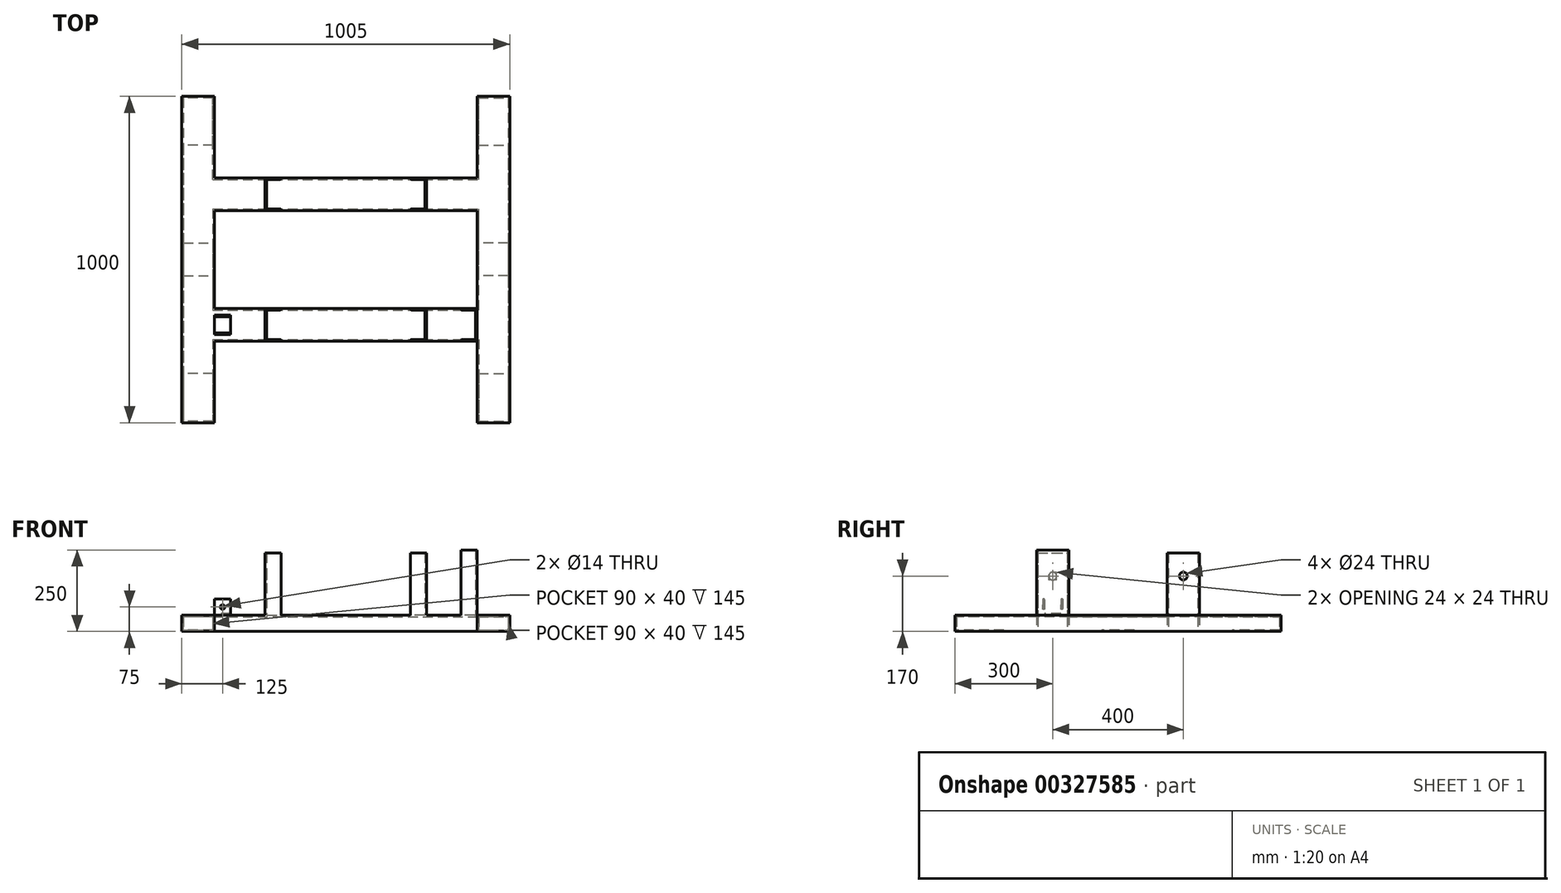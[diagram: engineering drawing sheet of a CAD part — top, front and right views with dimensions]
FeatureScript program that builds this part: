
annotation { "Feature Type Name" : "Feature", "Feature Type Description" : "" }
export const myFeature = defineFeature(function(context is Context, id is Id, definition is map)
    precondition{}
    {
        {
            var Q0;
            Q0=qCreatedBy(makeId("Top.planeOp"),FACE);
            var sketch = newSketch(context, id + "F0", { "sketchPlane" : qUnion([Q0])});
            skLineSegment(sketch, "E0", {"start": v(-402.5, 150) * mm, "end": v(402.5, 150) * mm});
            skLineSegment(sketch, "E1", {"start": v(0, 0) * mm, "end": v(0, 150) * mm, "construction": true});
            skPoint(sketch, "E2", {"position": v(0, 150) * mm});
            skLineSegment(sketch, "E3.0", {"start": v(-402.5, 250) * mm, "end": v(402.5, 250) * mm});
            skLineSegment(sketch, "E4", {"start": v(402.5, 0) * mm, "end": v(402.5, 500) * mm});
            skLineSegment(sketch, "E5", {"start": v(402.5, 500) * mm, "end": v(502.5, 500) * mm});
            skLineSegment(sketch, "E6", {"start": v(502.5, 500) * mm, "end": v(502.5, 0) * mm});
            skLineSegment(sketch, "E7.MirrorCS", {"start": v(-402.5, 0) * mm, "end": v(-402.5, 500) * mm});
            skLineSegment(sketch, "E8.MirrorCS", {"start": v(-502.5, 500) * mm, "end": v(-502.5, 0) * mm});
            skLineSegment(sketch, "E9.MirrorCS", {"start": v(-402.5, 500) * mm, "end": v(-502.5, 500) * mm});
            skLineSegment(sketch, "E10.MirrorCS", {"start": v(-402.5, 0) * mm, "end": v(-402.5, -500) * mm});
            skLineSegment(sketch, "E11.MirrorCS", {"start": v(-502.5, -500) * mm, "end": v(-502.5, 0) * mm});
            skLineSegment(sketch, "E12.MirrorCS", {"start": v(-402.5, -500) * mm, "end": v(-502.5, -500) * mm});
            skLineSegment(sketch, "E13.MirrorCS", {"start": v(-402.5, -250) * mm, "end": v(402.5, -250) * mm});
            skLineSegment(sketch, "E14.MirrorCS", {"start": v(-402.5, -150) * mm, "end": v(402.5, -150) * mm});
            skLineSegment(sketch, "E15.MirrorCS", {"start": v(402.5, 0) * mm, "end": v(402.5, -500) * mm});
            skLineSegment(sketch, "E16.MirrorCS", {"start": v(502.5, -500) * mm, "end": v(502.5, 0) * mm});
            skLineSegment(sketch, "E17.MirrorCS", {"start": v(402.5, -500) * mm, "end": v(502.5, -500) * mm});
            skLineSegment(sketch, "E18.bottom", {"start": v(502.5, 50) * mm, "end": v(402.5, 50) * mm});
            skLineSegment(sketch, "E18.top", {"start": v(502.5, -50) * mm, "end": v(402.5, -50) * mm});
            skLineSegment(sketch, "E18.left", {"start": v(502.5, 50) * mm, "end": v(502.5, -50) * mm});
            skLineSegment(sketch, "E18.right", {"start": v(402.5, 50) * mm, "end": v(402.5, -50) * mm});
            skPoint(sketch, "E18.middle", {"position": v(452.5, 0) * mm});
            skPoint(sketch, "E18.middle.positionSnap0", {"position": v(452.5, 500) * mm});
            skPoint(sketch, "E18.centerSnap0", {"position": v(452.5, 500) * mm});
            skLineSegment(sketch, "E19", {"start": v(402.5, 350) * mm, "end": v(502.5, 350) * mm});
            skLineSegment(sketch, "E20.MirrorCS", {"start": v(402.5, -350) * mm, "end": v(502.5, -350) * mm});
            skLineSegment(sketch, "E21.MirrorCS", {"start": v(-402.5, -350) * mm, "end": v(-502.5, -350) * mm});
            skLineSegment(sketch, "E22.MirrorCS", {"start": v(-502.5, -50) * mm, "end": v(-402.5, -50) * mm});
            skLineSegment(sketch, "E23.MirrorCS", {"start": v(-502.5, 50) * mm, "end": v(-402.5, 50) * mm});
            skLineSegment(sketch, "E24.MirrorCS", {"start": v(-402.5, 350) * mm, "end": v(-502.5, 350) * mm});
            skPoint(sketch, "E25.orphan", {"position": v(40.25, 250) * mm});
            skPoint(sketch, "E26.orphan", {"position": v(-40.25, 250) * mm});
            skPoint(sketch, "E27.orphan", {"position": v(40.25, -250) * mm});
            skPoint(sketch, "E28.orphan", {"position": v(-40.25, -250) * mm});
            skSolve(sketch);
        }
        {
            var Q0;
            Q0 = qSketchRegion(id + "F0", true);
            extrude(context, id + "F1", {"entities" : qUnion([Q0]), "depth" : 50 * mm});
        }
        {
            var Q0;
            Q0=makeQuery(id+"F1.opExtrude","CAP_FACE",FACE,{"disambiguationData":[OSD([sQuery(id+"F0.wireOp",EDGE,"E0"),sQuery(id+"F0.wireOp",EDGE,"E3.0"),sQuery(id+"F0.wireOp",EDGE,"E4"),sQuery(id+"F0.wireOp",EDGE,"E5"),sQuery(id+"F0.wireOp",EDGE,"E6"),sQuery(id+"F0.wireOp",EDGE,"E7.MirrorCS"),sQuery(id+"F0.wireOp",EDGE,"E8.MirrorCS"),sQuery(id+"F0.wireOp",EDGE,"E9.MirrorCS"),sQuery(id+"F0.wireOp",EDGE,"E10.MirrorCS"),sQuery(id+"F0.wireOp",EDGE,"E11.MirrorCS"),sQuery(id+"F0.wireOp",EDGE,"E12.MirrorCS"),sQuery(id+"F0.wireOp",EDGE,"E13.MirrorCS"),sQuery(id+"F0.wireOp",EDGE,"E14.MirrorCS"),sQuery(id+"F0.wireOp",EDGE,"E15.MirrorCS"),sQuery(id+"F0.wireOp",EDGE,"E16.MirrorCS"),sQuery(id+"F0.wireOp",EDGE,"E17.MirrorCS"),sQuery(id+"F0.wireOp",EDGE,"E18.left"),sQuery(id+"F0.wireOp",EDGE,"E18.right")])],"isStart":true});
            shell(context, id + "F2", {"entities" : qUnion([Q0]), "thickness" : 5 * mm});
        }
        {
            var Q0;
            {var subQ0=sQuery(id+"F0.wireOp",EDGE,"E12.MirrorCS");Q0=makeQuery(id+"F0.imprint","IMPRINT",FACE,{"disambiguationData":[TD([[makeQuery(id+"F0.imprint","IMPRINT",EDGE,{"derivedFrom":subQ0}),-1.0]])]});}
            var Q1;
            {var subQ3=sQuery(id+"F0.wireOp",EDGE,"E22.MirrorCS");Q1=makeQuery(id+"F0.imprint","IMPRINT",FACE,{"disambiguationData":[TD([[makeQuery(id+"F0.imprint","IMPRINT",EDGE,{"derivedFrom":subQ3}),1.0]])]});}
            var Q2;
            {var subQ0=sQuery(id+"F0.wireOp",EDGE,"E9.MirrorCS");Q2=makeQuery(id+"F0.imprint","IMPRINT",FACE,{"disambiguationData":[TD([[makeQuery(id+"F0.imprint","IMPRINT",EDGE,{"derivedFrom":subQ0}),1.0]])]});}
            var Q3;
            {var subQ0=sQuery(id+"F0.wireOp",EDGE,"E17.MirrorCS");Q3=makeQuery(id+"F0.imprint","IMPRINT",FACE,{"disambiguationData":[TD([[makeQuery(id+"F0.imprint","IMPRINT",EDGE,{"derivedFrom":subQ0}),1.0]])]});}
            var Q4;
            Q4=makeQuery(id+"F0.imprint","IMPRINT",FACE,{"disambiguationData":[TD([[makeQuery(id+"F0.imprint","IMPRINT",EDGE,{"derivedFrom":sQuery(id+"F0.wireOp",EDGE,"E18.bottom")}),1.0]])]});
            var Q5;
            {var subQ0=sQuery(id+"F0.wireOp",EDGE,"E5");Q5=makeQuery(id+"F0.imprint","IMPRINT",FACE,{"disambiguationData":[TD([[makeQuery(id+"F0.imprint","IMPRINT",EDGE,{"derivedFrom":subQ0}),-1.0]])]});}
            extrude(context, id + "F3", {"entities" : qUnion([Q0, Q1, Q2, Q3, Q4, Q5]), "operationType" : NewBodyOperationType.ADD, "depth" : 5 * mm});
        }
        {
            var Q0;
            Q0=makeQuery(id+"F1.opExtrude","CAP_FACE",FACE,{"disambiguationData":[OSD([sQuery(id+"F0.wireOp",EDGE,"E0"),sQuery(id+"F0.wireOp",EDGE,"E3.0"),sQuery(id+"F0.wireOp",EDGE,"E4"),sQuery(id+"F0.wireOp",EDGE,"E5"),sQuery(id+"F0.wireOp",EDGE,"E6"),sQuery(id+"F0.wireOp",EDGE,"E7.MirrorCS"),sQuery(id+"F0.wireOp",EDGE,"E8.MirrorCS"),sQuery(id+"F0.wireOp",EDGE,"E9.MirrorCS"),sQuery(id+"F0.wireOp",EDGE,"E10.MirrorCS"),sQuery(id+"F0.wireOp",EDGE,"E11.MirrorCS"),sQuery(id+"F0.wireOp",EDGE,"E12.MirrorCS"),sQuery(id+"F0.wireOp",EDGE,"E13.MirrorCS"),sQuery(id+"F0.wireOp",EDGE,"E14.MirrorCS"),sQuery(id+"F0.wireOp",EDGE,"E15.MirrorCS"),sQuery(id+"F0.wireOp",EDGE,"E16.MirrorCS"),sQuery(id+"F0.wireOp",EDGE,"E17.MirrorCS"),sQuery(id+"F0.wireOp",EDGE,"E18.left"),sQuery(id+"F0.wireOp",EDGE,"E18.right")])],"isStart":false});
            var sketch = newSketch(context, id + "F4", { "sketchPlane" : qUnion([Q0])});
            skLineSegment(sketch, "E29.bottom", {"start": v(248, 250) * mm, "end": v(-248, 250) * mm, "construction": true});
            skLineSegment(sketch, "E29.top", {"start": v(198, -250) * mm, "end": v(-248, -250) * mm, "construction": true});
            skLineSegment(sketch, "E29.left", {"start": v(248, 250) * mm, "end": v(248, -150) * mm, "construction": true});
            skLineSegment(sketch, "E29.right", {"start": v(-248, 250) * mm, "end": v(-248, -250) * mm, "construction": true});
            skPoint(sketch, "E29.middle", {"position": v(0, 0) * mm});
            skLineSegment(sketch, "E30.bottom", {"start": v(248, -250) * mm, "end": v(198, -250) * mm});
            skLineSegment(sketch, "E30.top", {"start": v(248, -150) * mm, "end": v(198, -150) * mm});
            skLineSegment(sketch, "E30.left", {"start": v(248, -250) * mm, "end": v(248, -150) * mm});
            skLineSegment(sketch, "E30.right", {"start": v(198, -250) * mm, "end": v(198, -249) * mm});
            skLineSegment(sketch, "E31.0", {"start": v(243, -155) * mm, "end": v(202, -155) * mm});
            skLineSegment(sketch, "E31.1", {"start": v(243, -245) * mm, "end": v(243, -155) * mm});
            skLineSegment(sketch, "E31.2", {"start": v(243, -245) * mm, "end": v(202, -245) * mm});
            skLineSegment(sketch, "E32.trimOffspring", {"start": v(198, -151) * mm, "end": v(198, -150) * mm});
            skPoint(sketch, "E33.visualSharp", {"position": v(198, -155) * mm});
            skArc(sketch, "E33.filletArc", {"start": v(198, -151) * mm, "mid": v(199.17, -153.83) * mm, "end": v(202, -155) * mm});
            skPoint(sketch, "E34.visualSharp", {"position": v(198, -245) * mm});
            skArc(sketch, "E34.filletArc", {"start": v(202, -245) * mm, "mid": v(199.17, -246.17) * mm, "end": v(198, -249) * mm});
            skSolve(sketch);
        }
        {
            var Q0;
            Q0 = qSketchRegion(id + "F4", true);
            extrude(context, id + "F5", {"entities" : qUnion([Q0]), "depth" : 190 * mm});
        }
        {
            var Q0;
            Q0=makeQuery(id+"F5.opExtrude","SWEPT_FACE",FACE,{"disambiguationData":[OSD([sQuery(id+"F4.wireOp",EDGE,"E30.left")])]});
            var sketch = newSketch(context, id + "F6", { "sketchPlane" : qUnion([Q0])});
            skLineSegment(sketch, "E35", {"start": v(-200, 50) * mm, "end": v(-200, 240) * mm, "construction": true});
            skPoint(sketch, "E36", {"position": v(-200, 170) * mm});
            skSolve(sketch);
        }
        {
            var Q0;
            Q0=sQuery(id+"F6.wireOp",VERTEX,"E36");
            var Q1;
            Q1=makeQuery(id+"F5.opExtrude","SWEPT_BODY",BODY,{"disambiguationData":[OSD([sQuery(id+"F4.wireOp",EDGE,"E30.bottom"),sQuery(id+"F4.wireOp",EDGE,"E30.top"),sQuery(id+"F4.wireOp",EDGE,"E30.left"),sQuery(id+"F4.wireOp",EDGE,"E30.right"),sQuery(id+"F4.wireOp",EDGE,"E31.0"),sQuery(id+"F4.wireOp",EDGE,"E31.1"),sQuery(id+"F4.wireOp",EDGE,"E31.2"),sQuery(id+"F4.wireOp",EDGE,"E32.trimOffspring"),sQuery(id+"F4.wireOp",EDGE,"E33.filletArc"),sQuery(id+"F4.wireOp",EDGE,"E34.filletArc")])]});
            hole(context, id + "F7", {"style" : HoleStyle.SIMPLE, "endStyle" : HoleEndStyle.THROUGH, "holeDiameter" : 24 * mm, "tappedDepth" : 12 * mm, "tapClearance" : 3, "locations" : qUnion([Q0]), "scope" : qUnion([Q1])});
        }
        {
            var Q0;
            Q0=makeQuery(id+"F5.opExtrude","SWEPT_BODY",BODY,{"disambiguationData":[OSD([sQuery(id+"F4.wireOp",EDGE,"E30.bottom"),sQuery(id+"F4.wireOp",EDGE,"E30.top"),sQuery(id+"F4.wireOp",EDGE,"E30.left"),sQuery(id+"F4.wireOp",EDGE,"E30.right"),sQuery(id+"F4.wireOp",EDGE,"E31.0"),sQuery(id+"F4.wireOp",EDGE,"E31.1"),sQuery(id+"F4.wireOp",EDGE,"E31.2"),sQuery(id+"F4.wireOp",EDGE,"E32.trimOffspring"),sQuery(id+"F4.wireOp",EDGE,"E33.filletArc"),sQuery(id+"F4.wireOp",EDGE,"E34.filletArc")])]});
            var Q1;
            Q1=qCreatedBy(makeId("Right.planeOp"),FACE);
            mirror(context, id + "F8", {"entities" : qUnion([Q0]), "mirrorPlane" : qUnion([Q1])});
        }
        {
            var Q0;
            Q0=makeQuery(id+"F5.opExtrude","SWEPT_BODY",BODY,{"disambiguationData":[OSD([sQuery(id+"F4.wireOp",EDGE,"E30.bottom"),sQuery(id+"F4.wireOp",EDGE,"E30.top"),sQuery(id+"F4.wireOp",EDGE,"E30.left"),sQuery(id+"F4.wireOp",EDGE,"E30.right"),sQuery(id+"F4.wireOp",EDGE,"E31.0"),sQuery(id+"F4.wireOp",EDGE,"E31.1"),sQuery(id+"F4.wireOp",EDGE,"E31.2"),sQuery(id+"F4.wireOp",EDGE,"E32.trimOffspring"),sQuery(id+"F4.wireOp",EDGE,"E33.filletArc"),sQuery(id+"F4.wireOp",EDGE,"E34.filletArc")])]});
            var Q1;
            Q1=makeQuery(id+"F8.opPattern","COPY",BODY,{"derivedFrom":makeQuery(id+"F5.opExtrude","SWEPT_BODY",BODY,{"disambiguationData":[OSD([sQuery(id+"F4.wireOp",EDGE,"E30.bottom"),sQuery(id+"F4.wireOp",EDGE,"E30.top"),sQuery(id+"F4.wireOp",EDGE,"E30.left"),sQuery(id+"F4.wireOp",EDGE,"E30.right"),sQuery(id+"F4.wireOp",EDGE,"E31.0"),sQuery(id+"F4.wireOp",EDGE,"E31.1"),sQuery(id+"F4.wireOp",EDGE,"E31.2"),sQuery(id+"F4.wireOp",EDGE,"E32.trimOffspring"),sQuery(id+"F4.wireOp",EDGE,"E33.filletArc"),sQuery(id+"F4.wireOp",EDGE,"E34.filletArc")])]}),"instanceName":"1"});
            var Q2;
            Q2=qCreatedBy(makeId("Front.planeOp"),FACE);
            mirror(context, id + "F9", {"entities" : qUnion([Q0, Q1]), "mirrorPlane" : qUnion([Q2])});
        }
        {
            var Q0;
            Q0=makeQuery(id+"F8.opPattern","COPY",BODY,{"derivedFrom":makeQuery(id+"F5.opExtrude","SWEPT_BODY",BODY,{"disambiguationData":[OSD([sQuery(id+"F4.wireOp",EDGE,"E30.bottom"),sQuery(id+"F4.wireOp",EDGE,"E30.top"),sQuery(id+"F4.wireOp",EDGE,"E30.left"),sQuery(id+"F4.wireOp",EDGE,"E30.right"),sQuery(id+"F4.wireOp",EDGE,"E31.0"),sQuery(id+"F4.wireOp",EDGE,"E31.1"),sQuery(id+"F4.wireOp",EDGE,"E31.2"),sQuery(id+"F4.wireOp",EDGE,"E32.trimOffspring"),sQuery(id+"F4.wireOp",EDGE,"E33.filletArc"),sQuery(id+"F4.wireOp",EDGE,"E34.filletArc")])]}),"instanceName":"1"});
            var Q1;
            Q1=makeQuery(id+"F9.opPattern","COPY",BODY,{"derivedFrom":makeQuery(id+"F8.opPattern","COPY",BODY,{"derivedFrom":makeQuery(id+"F5.opExtrude","SWEPT_BODY",BODY,{"disambiguationData":[OSD([sQuery(id+"F4.wireOp",EDGE,"E30.bottom"),sQuery(id+"F4.wireOp",EDGE,"E30.top"),sQuery(id+"F4.wireOp",EDGE,"E30.left"),sQuery(id+"F4.wireOp",EDGE,"E30.right"),sQuery(id+"F4.wireOp",EDGE,"E31.0"),sQuery(id+"F4.wireOp",EDGE,"E31.1"),sQuery(id+"F4.wireOp",EDGE,"E31.2"),sQuery(id+"F4.wireOp",EDGE,"E32.trimOffspring"),sQuery(id+"F4.wireOp",EDGE,"E33.filletArc"),sQuery(id+"F4.wireOp",EDGE,"E34.filletArc")])]}),"instanceName":"1"}),"instanceName":"1"});
            var Q2;
            Q2=makeQuery(id+"F5.opExtrude","SWEPT_BODY",BODY,{"disambiguationData":[OSD([sQuery(id+"F4.wireOp",EDGE,"E30.bottom"),sQuery(id+"F4.wireOp",EDGE,"E30.top"),sQuery(id+"F4.wireOp",EDGE,"E30.left"),sQuery(id+"F4.wireOp",EDGE,"E30.right"),sQuery(id+"F4.wireOp",EDGE,"E31.0"),sQuery(id+"F4.wireOp",EDGE,"E31.1"),sQuery(id+"F4.wireOp",EDGE,"E31.2"),sQuery(id+"F4.wireOp",EDGE,"E32.trimOffspring"),sQuery(id+"F4.wireOp",EDGE,"E33.filletArc"),sQuery(id+"F4.wireOp",EDGE,"E34.filletArc")])]});
            var Q3;
            Q3=makeQuery(id+"F9.opPattern","COPY",BODY,{"derivedFrom":makeQuery(id+"F5.opExtrude","SWEPT_BODY",BODY,{"disambiguationData":[OSD([sQuery(id+"F4.wireOp",EDGE,"E30.bottom"),sQuery(id+"F4.wireOp",EDGE,"E30.top"),sQuery(id+"F4.wireOp",EDGE,"E30.left"),sQuery(id+"F4.wireOp",EDGE,"E30.right"),sQuery(id+"F4.wireOp",EDGE,"E31.0"),sQuery(id+"F4.wireOp",EDGE,"E31.1"),sQuery(id+"F4.wireOp",EDGE,"E31.2"),sQuery(id+"F4.wireOp",EDGE,"E32.trimOffspring"),sQuery(id+"F4.wireOp",EDGE,"E33.filletArc"),sQuery(id+"F4.wireOp",EDGE,"E34.filletArc")])]}),"instanceName":"1"});
            var Q4;
            Q4=makeQuery(id+"F1.opExtrude","SWEPT_BODY",BODY,{"disambiguationData":[OSD([sQuery(id+"F0.wireOp",EDGE,"E0"),sQuery(id+"F0.wireOp",EDGE,"E3.0"),sQuery(id+"F0.wireOp",EDGE,"E4"),sQuery(id+"F0.wireOp",EDGE,"E5"),sQuery(id+"F0.wireOp",EDGE,"E6"),sQuery(id+"F0.wireOp",EDGE,"E7.MirrorCS"),sQuery(id+"F0.wireOp",EDGE,"E8.MirrorCS"),sQuery(id+"F0.wireOp",EDGE,"E9.MirrorCS"),sQuery(id+"F0.wireOp",EDGE,"E10.MirrorCS"),sQuery(id+"F0.wireOp",EDGE,"E11.MirrorCS"),sQuery(id+"F0.wireOp",EDGE,"E12.MirrorCS"),sQuery(id+"F0.wireOp",EDGE,"E13.MirrorCS"),sQuery(id+"F0.wireOp",EDGE,"E14.MirrorCS"),sQuery(id+"F0.wireOp",EDGE,"E15.MirrorCS"),sQuery(id+"F0.wireOp",EDGE,"E16.MirrorCS"),sQuery(id+"F0.wireOp",EDGE,"E17.MirrorCS"),sQuery(id+"F0.wireOp",EDGE,"E18.left"),sQuery(id+"F0.wireOp",EDGE,"E18.right")])]});
            booleanBodies(context, id + "F10", {"operationType" : BooleanOperationType.UNION, "tools" : qUnion([Q0, Q1, Q2, Q3, Q4])});
        }
        {
            var Q0;
            {var subQ0=sQuery(id+"F0.wireOp",EDGE,"E14.MirrorCS");var subQ1=sQuery(id+"F0.wireOp",EDGE,"E12.MirrorCS");var subQ4=sQuery(id+"F0.wireOp",EDGE,"E10.MirrorCS");var subQ5=sQuery(id+"F0.wireOp",EDGE,"E11.MirrorCS");var subQ6=sQuery(id+"F0.wireOp",EDGE,"E8.MirrorCS");var subQ9=sQuery(id+"F0.wireOp",EDGE,"E9.MirrorCS");var subQ10=sQuery(id+"F0.wireOp",EDGE,"E0");var subQ11=sQuery(id+"F0.wireOp",EDGE,"E13.MirrorCS");var subQ12=sQuery(id+"F0.wireOp",EDGE,"E3.0");var subQ13=sQuery(id+"F0.wireOp",EDGE,"E7.MirrorCS");Q0=makeQuery(id+"F10.opBoolean","SPLIT",FACE,{"disambiguationData":[TD([makeQuery(id+"F1.opExtrude","SWEPT_FACE",FACE,{"disambiguationData":[OSD([subQ13])]})])],"derivedFrom":makeQuery(id+"F1.opExtrude","CAP_FACE",FACE,{"disambiguationData":[OSD([subQ10,subQ12,sQuery(id+"F0.wireOp",EDGE,"E4"),sQuery(id+"F0.wireOp",EDGE,"E5"),sQuery(id+"F0.wireOp",EDGE,"E6"),subQ13,subQ6,subQ9,subQ4,subQ5,subQ1,subQ11,subQ0,sQuery(id+"F0.wireOp",EDGE,"E15.MirrorCS"),sQuery(id+"F0.wireOp",EDGE,"E16.MirrorCS"),sQuery(id+"F0.wireOp",EDGE,"E17.MirrorCS"),sQuery(id+"F0.wireOp",EDGE,"E18.left"),sQuery(id+"F0.wireOp",EDGE,"E18.right")])],"isStart":false})});}
            var sketch = newSketch(context, id + "F11", { "sketchPlane" : qUnion([Q0])});
            skLineSegment(sketch, "E37.bottom", {"start": v(-352.5, -170) * mm, "end": v(-402.5, -170) * mm});
            skLineSegment(sketch, "E37.top", {"start": v(-352.5, -230) * mm, "end": v(-402.5, -230) * mm});
            skLineSegment(sketch, "E37.left", {"start": v(-352.5, -170) * mm, "end": v(-352.5, -230) * mm});
            skLineSegment(sketch, "E37.right", {"start": v(-402.5, -170) * mm, "end": v(-402.5, -230) * mm});
            skPoint(sketch, "E37.middle", {"position": v(-377.5, -200) * mm});
            skPoint(sketch, "E37.middle.positionSnap0", {"position": v(-248, -200) * mm});
            skPoint(sketch, "E37.centerSnap0", {"position": v(-248, -200) * mm});
            skLineSegment(sketch, "E38.0", {"start": v(-352.5, -175) * mm, "end": v(-402.5, -175) * mm});
            skLineSegment(sketch, "E39.0", {"start": v(-352.5, -225) * mm, "end": v(-402.5, -225) * mm});
            skPoint(sketch, "E40.firstSnap0", {"position": v(-325.25, -150) * mm});
            skPoint(sketch, "E40.oppositeSnap0", {"position": v(-325.25, -250) * mm});
            skLineSegment(sketch, "E40.bottom", {"start": v(402.5, -150) * mm, "end": v(352.5, -150) * mm});
            skLineSegment(sketch, "E40.top", {"start": v(402.5, -250) * mm, "end": v(352.5, -250) * mm});
            skLineSegment(sketch, "E40.left", {"start": v(402.5, -150) * mm, "end": v(402.5, -250) * mm});
            skLineSegment(sketch, "E40.right", {"start": v(352.5, -150) * mm, "end": v(352.5, -151) * mm});
            skLineSegment(sketch, "E41.0", {"start": v(397.5, -155) * mm, "end": v(356.5, -155) * mm});
            skLineSegment(sketch, "E41.1", {"start": v(397.5, -155) * mm, "end": v(397.5, -245) * mm});
            skLineSegment(sketch, "E41.2", {"start": v(397.5, -245) * mm, "end": v(356.5, -245) * mm});
            skLineSegment(sketch, "E42.trimOffspring", {"start": v(352.5, -249) * mm, "end": v(352.5, -250) * mm});
            skPoint(sketch, "E43.visualSharp", {"position": v(352.5, -155) * mm});
            skArc(sketch, "E43.filletArc", {"start": v(352.5, -151) * mm, "mid": v(353.67, -153.83) * mm, "end": v(356.5, -155) * mm});
            skPoint(sketch, "E44.visualSharp", {"position": v(352.5, -245) * mm});
            skArc(sketch, "E44.filletArc", {"start": v(356.5, -245) * mm, "mid": v(353.67, -246.17) * mm, "end": v(352.5, -249) * mm});
            skSolve(sketch);
        }
        {
            var Q0;
            {var subQ0=sQuery(id+"F11.wireOp",EDGE,"E38.0");Q0=makeQuery(id+"F11.imprint","IMPRINT",FACE,{"disambiguationData":[TD([[makeQuery(id+"F11.imprint","IMPRINT",EDGE,{"derivedFrom":subQ0}),1.0]])]});}
            extrude(context, id + "F12", {"entities" : qUnion([Q0]), "operationType" : NewBodyOperationType.ADD, "depth" : 5 * mm});
        }
        {
            var Q0;
            {var subQ0=sQuery(id+"F11.wireOp",EDGE,"E37.top");Q0=makeQuery(id+"F11.imprint","IMPRINT",FACE,{"disambiguationData":[TD([[makeQuery(id+"F11.imprint","IMPRINT",EDGE,{"derivedFrom":subQ0}),-1.0]])]});}
            var Q1;
            {var subQ0=sQuery(id+"F11.wireOp",EDGE,"E37.bottom");Q1=makeQuery(id+"F11.imprint","IMPRINT",FACE,{"disambiguationData":[TD([[makeQuery(id+"F11.imprint","IMPRINT",EDGE,{"derivedFrom":subQ0}),1.0]])]});}
            extrude(context, id + "F13", {"entities" : qUnion([Q0, Q1]), "operationType" : NewBodyOperationType.ADD, "depth" : 50 * mm});
        }
        {
            var Q0;
            Q0=makeQuery(id+"F11.imprint","IMPRINT",FACE,{"disambiguationData":[TD([[makeQuery(id+"F11.imprint","IMPRINT",EDGE,{"derivedFrom":sQuery(id+"F11.wireOp",EDGE,"E40.bottom")}),1.0]])]});
            extrude(context, id + "F14", {"entities" : qUnion([Q0]), "operationType" : NewBodyOperationType.ADD, "depth" : 200 * mm});
        }
        {
            var Q0;
            Q0=makeQuery(id+"F13.opExtrude","SWEPT_FACE",FACE,{"disambiguationData":[OSD([sQuery(id+"F11.wireOp",EDGE,"E37.top")])]});
            var sketch = newSketch(context, id + "F15", { "sketchPlane" : qUnion([Q0])});
            skPoint(sketch, "E45", {"position": v(-377.5, 75) * mm});
            skPoint(sketch, "E45.positionSnap0", {"position": v(-402.5, 75) * mm});
            skPoint(sketch, "E45.positionSnap1", {"position": v(-377.5, 50) * mm});
            skSolve(sketch);
        }
        {
            var Q0;
            Q0=sQuery(id+"F15.wireOp",VERTEX,"E45");
            var Q1;
            Q1=makeQuery(id+"F8.opPattern","COPY",BODY,{"derivedFrom":makeQuery(id+"F5.opExtrude","SWEPT_BODY",BODY,{"disambiguationData":[OSD([sQuery(id+"F4.wireOp",EDGE,"E30.bottom"),sQuery(id+"F4.wireOp",EDGE,"E30.top"),sQuery(id+"F4.wireOp",EDGE,"E30.left"),sQuery(id+"F4.wireOp",EDGE,"E30.right"),sQuery(id+"F4.wireOp",EDGE,"E31.0"),sQuery(id+"F4.wireOp",EDGE,"E31.1"),sQuery(id+"F4.wireOp",EDGE,"E31.2"),sQuery(id+"F4.wireOp",EDGE,"E32.trimOffspring"),sQuery(id+"F4.wireOp",EDGE,"E33.filletArc"),sQuery(id+"F4.wireOp",EDGE,"E34.filletArc")])]}),"instanceName":"1"});
            hole(context, id + "F16", {"style" : HoleStyle.SIMPLE, "endStyle" : HoleEndStyle.THROUGH, "holeDiameter" : 14 * mm, "tappedDepth" : 12 * mm, "tapClearance" : 3, "locations" : qUnion([Q0]), "scope" : qUnion([Q1])});
        }
        {
            var Q0;
            Q0=makeQuery(id+"F12.opExtrude","CAP_EDGE",EDGE,{"disambiguationData":[OSD([sQuery(id+"F11.wireOp",EDGE,"E38.0")])],"isStart":false});
            var Q1;
            Q1=makeQuery(id+"F12.opExtrude","CAP_EDGE",EDGE,{"disambiguationData":[OSD([sQuery(id+"F11.wireOp",EDGE,"E39.0")])],"isStart":false});
            var Q2;
            Q2=makeQuery(id+"F13.opExtrude","CAP_EDGE",EDGE,{"disambiguationData":[OSD([sQuery(id+"F11.wireOp",EDGE,"E39.0")])],"isStart":false});
            var Q3;
            Q3=makeQuery(id+"F13.opExtrude","CAP_EDGE",EDGE,{"disambiguationData":[OSD([sQuery(id+"F11.wireOp",EDGE,"E38.0")])],"isStart":false});
            var Q4;
            Q4=makeQuery(id+"F13.opExtrude","CAP_EDGE",EDGE,{"disambiguationData":[OSD([sQuery(id+"F11.wireOp",EDGE,"E37.top")])],"isStart":true});
            var Q5;
            {var subQ0=sQuery(id+"F11.wireOp",EDGE,"E37.right");Q5=makeQuery(id+"F13.boolean.opBoolean","MERGE",EDGE,{"derivedFrom":[makeQuery(id+"F12.opExtrude","CAP_EDGE",EDGE,{"disambiguationData":[OSD([subQ0])],"isStart":true}),makeQuery(id+"F13.opExtrude","CAP_EDGE",EDGE,{"disambiguationData":[OSD([subQ0]),TDD([makeQuery(id+"F11.imprint","IMPRINT",EDGE,{"disambiguationData":[TD([[makeQuery(id+"F11.imprint","INTERSECT",VERTEX,{"derivedFrom":[sQuery(id+"F11.wireOp",EDGE,"E37.bottom"),subQ0]}),-1.0]])],"derivedFrom":subQ0})])],"isStart":true}),makeQuery(id+"F13.opExtrude","CAP_EDGE",EDGE,{"disambiguationData":[OSD([subQ0]),TDD([makeQuery(id+"F11.imprint","IMPRINT",EDGE,{"disambiguationData":[TD([[makeQuery(id+"F11.imprint","INTERSECT",VERTEX,{"derivedFrom":[sQuery(id+"F11.wireOp",EDGE,"E37.top"),subQ0]}),1.0]])],"derivedFrom":subQ0})])],"isStart":true})]});}
            var Q6;
            Q6=makeQuery(id+"F13.opExtrude","CAP_EDGE",EDGE,{"disambiguationData":[OSD([sQuery(id+"F11.wireOp",EDGE,"E37.bottom")])],"isStart":true});
            var Q7;
            {var subQ0=sQuery(id+"F11.wireOp",EDGE,"E37.left");Q7=makeQuery(id+"F13.boolean.opBoolean","MERGE",EDGE,{"derivedFrom":[makeQuery(id+"F12.opExtrude","CAP_EDGE",EDGE,{"disambiguationData":[OSD([subQ0])],"isStart":true}),makeQuery(id+"F13.opExtrude","CAP_EDGE",EDGE,{"disambiguationData":[OSD([subQ0]),TDD([makeQuery(id+"F11.imprint","IMPRINT",EDGE,{"disambiguationData":[TD([[makeQuery(id+"F11.imprint","INTERSECT",VERTEX,{"derivedFrom":[sQuery(id+"F11.wireOp",EDGE,"E37.bottom"),subQ0]}),-1.0]])],"derivedFrom":subQ0})])],"isStart":true}),makeQuery(id+"F13.opExtrude","CAP_EDGE",EDGE,{"disambiguationData":[OSD([subQ0]),TDD([makeQuery(id+"F11.imprint","IMPRINT",EDGE,{"disambiguationData":[TD([[makeQuery(id+"F11.imprint","INTERSECT",VERTEX,{"derivedFrom":[sQuery(id+"F11.wireOp",EDGE,"E37.top"),subQ0]}),1.0]])],"derivedFrom":subQ0})])],"isStart":true})]});}
            var Q8;
            Q8=makeQuery(id+"F8.opPattern","COPY",EDGE,{"derivedFrom":makeQuery(id+"F5.opExtrude","CAP_EDGE",EDGE,{"disambiguationData":[OSD([sQuery(id+"F4.wireOp",EDGE,"E30.left")])],"isStart":true}),"instanceName":"1"});
            var Q9;
            Q9=makeQuery(id+"F9.opPattern","COPY",EDGE,{"derivedFrom":makeQuery(id+"F8.opPattern","COPY",EDGE,{"derivedFrom":makeQuery(id+"F5.opExtrude","CAP_EDGE",EDGE,{"disambiguationData":[OSD([sQuery(id+"F4.wireOp",EDGE,"E30.left")])],"isStart":true}),"instanceName":"1"}),"instanceName":"1"});
            var Q10;
            Q10=makeQuery(id+"F5.opExtrude","CAP_EDGE",EDGE,{"disambiguationData":[OSD([sQuery(id+"F4.wireOp",EDGE,"E31.1")])],"isStart":true});
            var Q11;
            Q11=makeQuery(id+"F5.opExtrude","CAP_EDGE",EDGE,{"disambiguationData":[OSD([sQuery(id+"F4.wireOp",EDGE,"E31.0")])],"isStart":true});
            var Q12;
            Q12=makeQuery(id+"F5.opExtrude","CAP_EDGE",EDGE,{"disambiguationData":[OSD([sQuery(id+"F4.wireOp",EDGE,"E33.filletArc")])],"isStart":true});
            var Q13;
            Q13=makeQuery(id+"F5.opExtrude","CAP_EDGE",EDGE,{"disambiguationData":[OSD([sQuery(id+"F4.wireOp",EDGE,"E31.2")])],"isStart":true});
            var Q14;
            Q14=makeQuery(id+"F5.opExtrude","CAP_EDGE",EDGE,{"disambiguationData":[OSD([sQuery(id+"F4.wireOp",EDGE,"E34.filletArc")])],"isStart":true});
            var Q15;
            Q15=makeQuery(id+"F9.opPattern","COPY",EDGE,{"derivedFrom":makeQuery(id+"F5.opExtrude","CAP_EDGE",EDGE,{"disambiguationData":[OSD([sQuery(id+"F4.wireOp",EDGE,"E31.2")])],"isStart":true}),"instanceName":"1"});
            var Q16;
            Q16=makeQuery(id+"F9.opPattern","COPY",EDGE,{"derivedFrom":makeQuery(id+"F5.opExtrude","CAP_EDGE",EDGE,{"disambiguationData":[OSD([sQuery(id+"F4.wireOp",EDGE,"E34.filletArc")])],"isStart":true}),"instanceName":"1"});
            var Q17;
            Q17=makeQuery(id+"F9.opPattern","COPY",EDGE,{"derivedFrom":makeQuery(id+"F5.opExtrude","CAP_EDGE",EDGE,{"disambiguationData":[OSD([sQuery(id+"F4.wireOp",EDGE,"E31.1")])],"isStart":true}),"instanceName":"1"});
            var Q18;
            Q18=makeQuery(id+"F9.opPattern","COPY",EDGE,{"derivedFrom":makeQuery(id+"F5.opExtrude","CAP_EDGE",EDGE,{"disambiguationData":[OSD([sQuery(id+"F4.wireOp",EDGE,"E31.0")])],"isStart":true}),"instanceName":"1"});
            var Q19;
            Q19=makeQuery(id+"F9.opPattern","COPY",EDGE,{"derivedFrom":makeQuery(id+"F5.opExtrude","CAP_EDGE",EDGE,{"disambiguationData":[OSD([sQuery(id+"F4.wireOp",EDGE,"E33.filletArc")])],"isStart":true}),"instanceName":"1"});
            var Q20;
            Q20=makeQuery(id+"F9.opPattern","COPY",EDGE,{"derivedFrom":makeQuery(id+"F5.opExtrude","CAP_EDGE",EDGE,{"disambiguationData":[OSD([sQuery(id+"F4.wireOp",EDGE,"E30.left")])],"isStart":true}),"instanceName":"1"});
            var Q21;
            Q21=makeQuery(id+"F5.opExtrude","CAP_EDGE",EDGE,{"disambiguationData":[OSD([sQuery(id+"F4.wireOp",EDGE,"E30.left")])],"isStart":true});
            var Q22;
            Q22=makeQuery(id+"F14.opExtrude","CAP_EDGE",EDGE,{"disambiguationData":[OSD([sQuery(id+"F11.wireOp",EDGE,"E41.0")])],"isStart":true});
            var Q23;
            Q23=makeQuery(id+"F14.opExtrude","CAP_EDGE",EDGE,{"disambiguationData":[OSD([sQuery(id+"F11.wireOp",EDGE,"E43.filletArc")])],"isStart":true});
            var Q24;
            Q24=makeQuery(id+"F14.opExtrude","CAP_EDGE",EDGE,{"disambiguationData":[OSD([sQuery(id+"F11.wireOp",EDGE,"E41.1")])],"isStart":true});
            var Q25;
            Q25=makeQuery(id+"F14.opExtrude","CAP_EDGE",EDGE,{"disambiguationData":[OSD([sQuery(id+"F11.wireOp",EDGE,"E41.2")])],"isStart":true});
            var Q26;
            Q26=makeQuery(id+"F14.opExtrude","CAP_EDGE",EDGE,{"disambiguationData":[OSD([sQuery(id+"F11.wireOp",EDGE,"E44.filletArc")])],"isStart":true});
            var Q27;
            Q27=makeQuery(id+"F14.opExtrude","CAP_EDGE",EDGE,{"disambiguationData":[OSD([sQuery(id+"F11.wireOp",EDGE,"E40.left")])],"isStart":true});
            var Q28;
            Q28=makeQuery(id+"F9.opPattern","COPY",EDGE,{"derivedFrom":makeQuery(id+"F8.opPattern","COPY",EDGE,{"derivedFrom":makeQuery(id+"F5.opExtrude","CAP_EDGE",EDGE,{"disambiguationData":[OSD([sQuery(id+"F4.wireOp",EDGE,"E31.0")])],"isStart":true}),"instanceName":"1"}),"instanceName":"1"});
            var Q29;
            Q29=makeQuery(id+"F9.opPattern","COPY",EDGE,{"derivedFrom":makeQuery(id+"F8.opPattern","COPY",EDGE,{"derivedFrom":makeQuery(id+"F5.opExtrude","CAP_EDGE",EDGE,{"disambiguationData":[OSD([sQuery(id+"F4.wireOp",EDGE,"E33.filletArc")])],"isStart":true}),"instanceName":"1"}),"instanceName":"1"});
            var Q30;
            Q30=makeQuery(id+"F9.opPattern","COPY",EDGE,{"derivedFrom":makeQuery(id+"F8.opPattern","COPY",EDGE,{"derivedFrom":makeQuery(id+"F5.opExtrude","CAP_EDGE",EDGE,{"disambiguationData":[OSD([sQuery(id+"F4.wireOp",EDGE,"E31.1")])],"isStart":true}),"instanceName":"1"}),"instanceName":"1"});
            var Q31;
            Q31=makeQuery(id+"F9.opPattern","COPY",EDGE,{"derivedFrom":makeQuery(id+"F8.opPattern","COPY",EDGE,{"derivedFrom":makeQuery(id+"F5.opExtrude","CAP_EDGE",EDGE,{"disambiguationData":[OSD([sQuery(id+"F4.wireOp",EDGE,"E31.2")])],"isStart":true}),"instanceName":"1"}),"instanceName":"1"});
            var Q32;
            Q32=makeQuery(id+"F9.opPattern","COPY",EDGE,{"derivedFrom":makeQuery(id+"F8.opPattern","COPY",EDGE,{"derivedFrom":makeQuery(id+"F5.opExtrude","CAP_EDGE",EDGE,{"disambiguationData":[OSD([sQuery(id+"F4.wireOp",EDGE,"E34.filletArc")])],"isStart":true}),"instanceName":"1"}),"instanceName":"1"});
            var Q33;
            Q33=makeQuery(id+"F8.opPattern","COPY",EDGE,{"derivedFrom":makeQuery(id+"F5.opExtrude","CAP_EDGE",EDGE,{"disambiguationData":[OSD([sQuery(id+"F4.wireOp",EDGE,"E31.0")])],"isStart":true}),"instanceName":"1"});
            var Q34;
            Q34=makeQuery(id+"F8.opPattern","COPY",EDGE,{"derivedFrom":makeQuery(id+"F5.opExtrude","CAP_EDGE",EDGE,{"disambiguationData":[OSD([sQuery(id+"F4.wireOp",EDGE,"E33.filletArc")])],"isStart":true}),"instanceName":"1"});
            var Q35;
            Q35=makeQuery(id+"F8.opPattern","COPY",EDGE,{"derivedFrom":makeQuery(id+"F5.opExtrude","CAP_EDGE",EDGE,{"disambiguationData":[OSD([sQuery(id+"F4.wireOp",EDGE,"E31.2")])],"isStart":true}),"instanceName":"1"});
            var Q36;
            Q36=makeQuery(id+"F8.opPattern","COPY",EDGE,{"derivedFrom":makeQuery(id+"F5.opExtrude","CAP_EDGE",EDGE,{"disambiguationData":[OSD([sQuery(id+"F4.wireOp",EDGE,"E34.filletArc")])],"isStart":true}),"instanceName":"1"});
            var Q37;
            Q37=makeQuery(id+"F8.opPattern","COPY",EDGE,{"derivedFrom":makeQuery(id+"F5.opExtrude","CAP_EDGE",EDGE,{"disambiguationData":[OSD([sQuery(id+"F4.wireOp",EDGE,"E31.1")])],"isStart":true}),"instanceName":"1"});
            fillet(context, id + "F17", {"entities" : qUnion([Q0, Q1, Q2, Q3, Q4, Q5, Q6, Q7, Q8, Q9, Q10, Q11, Q12, Q13, Q14, Q15, Q16, Q17, Q18, Q19, Q20, Q21, Q22, Q23, Q24, Q25, Q26, Q27, Q28, Q29, Q30, Q31, Q32, Q33, Q34, Q35, Q36, Q37]), "radius" : 2.5 * mm, "tangentPropagation" : true, "allowEdgeOverflow" : false});
        }
    });
